# Revit family: CeilingMount
name_source: partatom
category: Lighting Fixtures
revit_build: Autodesk Revit 2014 (Build: 20130308_1515(x64)
units: mm (PartAtom-declared; Revit-internal decimal feet)

## types (1)
- VTC
    Apparent Load = 0 VA
    Assembly Code = D5020200
    CCT = 5000K
    Color Filter = 16777215
    Colour = Hubbell - Gray
    Default Elevation = 48"
    Description = LED Vaportite, die cast housing, glass globe
    Dimming Lamp Color Temperature Shift = <None>
    Distribution = Type II
    Emit Shape Visible in Rendering = No
    Emit from Circle Diameter = 5 1/2"
    Glass = Glass - Hubbell - White
    Lamp = 1
    Load Classification = Lighting
    Manufacturer = Hubbell Industrial Lighting
    Model = VTC
    Photometric Notes = More IES files download in Photometrics Web Link
    Photometric Web File = VTC-5K-G-U-P2-G-GR.ies
    Photometrics Web Link = https://www.hubbell.com
    Pole Height = 120"
    Power Factor = 1
    Product Documentation Link = https://hubbellcdn.com
    Product Page URL = https://www.hubbell.com
    Tilt Angle = 90.00°
    Type Comments = Lighting Fixture
    URL = https://www.hubbell.com
    Voltage = 120 V
    Warranty = Five year limited warranty
    Wattage Comments = 27W

## geometry (parser evidence)
native form markers: Sweep x4
no freeform markers — native parametric forms only
